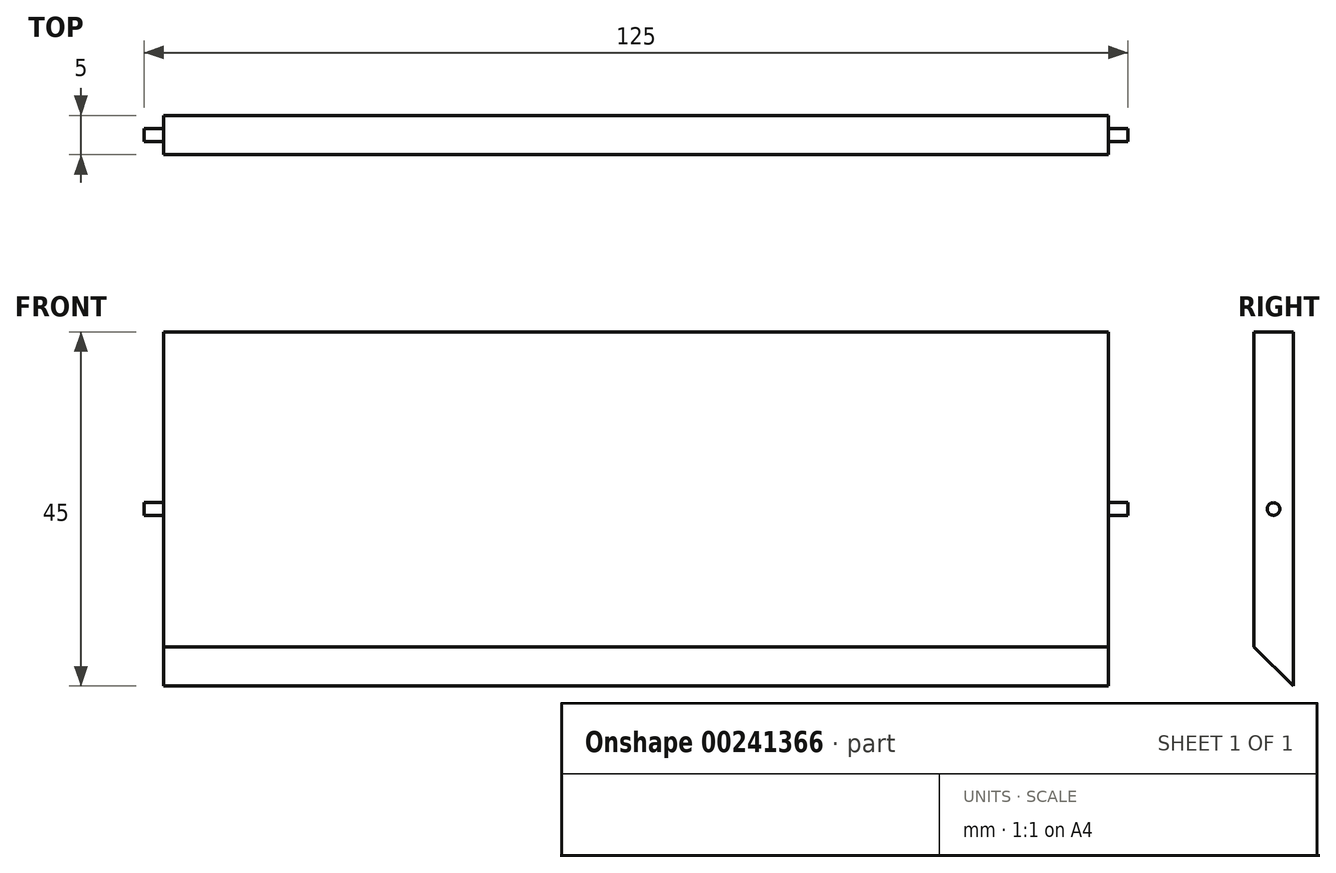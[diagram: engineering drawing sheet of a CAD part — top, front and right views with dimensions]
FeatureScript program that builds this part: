
annotation { "Feature Type Name" : "Feature", "Feature Type Description" : "" }
export const myFeature = defineFeature(function(context is Context, id is Id, definition is map)
    precondition{}
    {
        {
            var Q0;
            Q0=qCreatedBy(makeId("Right.planeOp"),FACE);
            var sketch = newSketch(context, id + "F0", { "sketchPlane" : qUnion([Q0])});
            skLineSegment(sketch, "E0.bottom", {"start": v(-2.5, 22.5) * mm, "end": v(2.5, 22.5) * mm});
            skLineSegment(sketch, "E0.top", {"start": v(-2.5, -22.5) * mm, "end": v(2.5, -22.5) * mm});
            skLineSegment(sketch, "E0.left", {"start": v(-2.5, 22.5) * mm, "end": v(-2.5, -22.5) * mm});
            skLineSegment(sketch, "E0.right", {"start": v(2.5, 22.5) * mm, "end": v(2.5, -22.5) * mm});
            skPoint(sketch, "E0.middle", {"position": v(0, 0) * mm});
            skSolve(sketch);
        }
        {
            var Q0;
            Q0 = qSketchRegion(id + "F0", true);
            extrude(context, id + "F1", {"entities" : qUnion([Q0]), "depth" : 120 * mm});
        }
        {
            var Q0;
            Q0=makeQuery(id+"F1.opExtrude","SWEPT_EDGE",EDGE,{"disambiguationData":[OSD([sQuery(id+"F0.wireOp",EDGE,"E0.top"),sQuery(id+"F0.wireOp",EDGE,"E0.left")])]});
            chamfer(context, id + "F2", {"entities" : qUnion([Q0]), "width" : 5 * mm, "tangentPropagation" : true});
        }
        {
            var Q0;
            Q0=makeQuery(id+"F1.opExtrude","CAP_FACE",FACE,{"disambiguationData":[OSD([sQuery(id+"F0.wireOp",EDGE,"E0.bottom"),sQuery(id+"F0.wireOp",EDGE,"E0.top"),sQuery(id+"F0.wireOp",EDGE,"E0.left"),sQuery(id+"F0.wireOp",EDGE,"E0.right")])],"isStart":true});
            var sketch = newSketch(context, id + "F3", { "sketchPlane" : qUnion([Q0])});
            skCircle(sketch, "E1", {"center": v(0, 0) * mm, "radius": 0.8 * mm});
            skSolve(sketch);
        }
        {
            var Q0;
            Q0 = qSketchRegion(id + "F3", true);
            extrude(context, id + "F4", {"entities" : qUnion([Q0]), "operationType" : NewBodyOperationType.ADD, "depth" : 2.5 * mm});
        }
        {
            var Q0;
            Q0=makeQuery(id+"F1.opExtrude","CAP_FACE",FACE,{"disambiguationData":[OSD([sQuery(id+"F0.wireOp",EDGE,"E0.bottom"),sQuery(id+"F0.wireOp",EDGE,"E0.top"),sQuery(id+"F0.wireOp",EDGE,"E0.left"),sQuery(id+"F0.wireOp",EDGE,"E0.right")])],"isStart":false});
            var sketch = newSketch(context, id + "F5", { "sketchPlane" : qUnion([Q0])});
            skCircle(sketch, "E2", {"center": v(0, 0) * mm, "radius": 0.8 * mm});
            skSolve(sketch);
        }
        {
            var Q0;
            Q0 = qSketchRegion(id + "F5", true);
            extrude(context, id + "F6", {"entities" : qUnion([Q0]), "operationType" : NewBodyOperationType.ADD, "depth" : 2.5 * mm});
        }
    });
